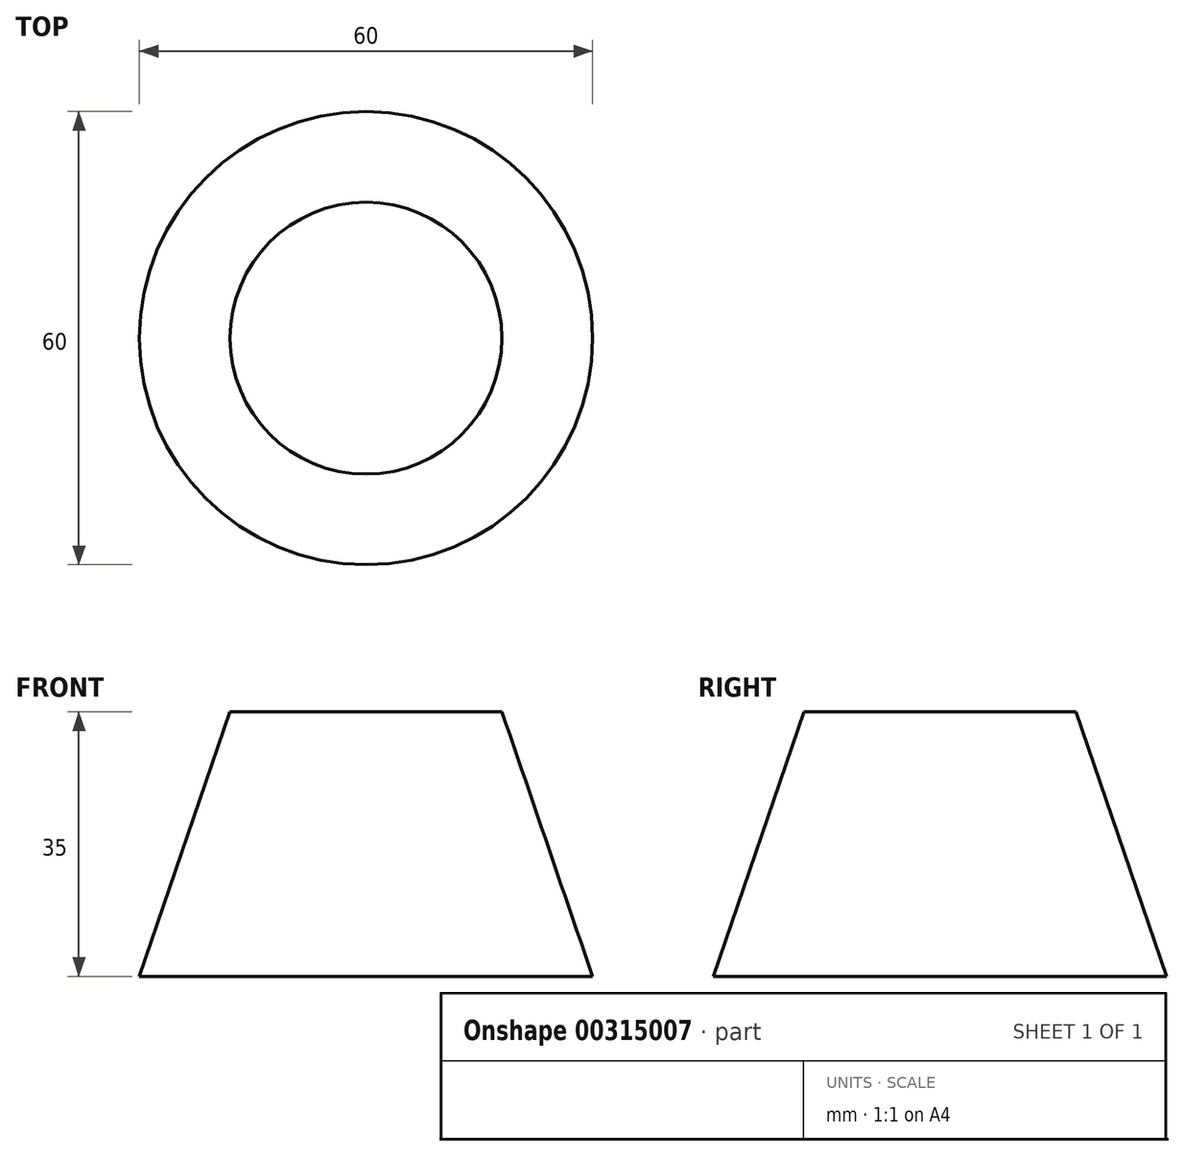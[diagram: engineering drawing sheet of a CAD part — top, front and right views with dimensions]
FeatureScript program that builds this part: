
annotation { "Feature Type Name" : "Feature", "Feature Type Description" : "" }
export const myFeature = defineFeature(function(context is Context, id is Id, definition is map)
    precondition{}
    {
        {
            var Q0;
            Q0=qCreatedBy(makeId("Front.planeOp"),FACE);
            var sketch = newSketch(context, id + "F0", { "sketchPlane" : qUnion([Q0])});
            skLineSegment(sketch, "E0", {"start": v(0, 0) * mm, "end": v(0, 35) * mm});
            skLineSegment(sketch, "E1", {"start": v(0, 35) * mm, "end": v(18, 35) * mm});
            skLineSegment(sketch, "E2", {"start": v(18, 35) * mm, "end": v(30, 0) * mm});
            skLineSegment(sketch, "E3", {"start": v(30, 0) * mm, "end": v(0, 0) * mm});
            skLineSegment(sketch, "E4", {"start": v(0, 45.82) * mm, "end": v(0, -6.77) * mm, "construction": true});
            skSolve(sketch);
        }
        {
            var Q0;
            Q0=makeQuery(id+"F0.imprint","IMPRINT",FACE,{"disambiguationData":[TD([[makeQuery(id+"F0.imprint","IMPRINT",EDGE,{"derivedFrom":sQuery(id+"F0.wireOp",EDGE,"E0")}),-1.0]])]});
            var Q1;
            Q1=sQuery(id+"F0.wireOp",EDGE,"E4");
            revolve(context, id + "F1", {"entities" : qUnion([Q0]), "axis" : qUnion([Q1]), "revolveType" : RevolveType.FULL});
        }
    });
